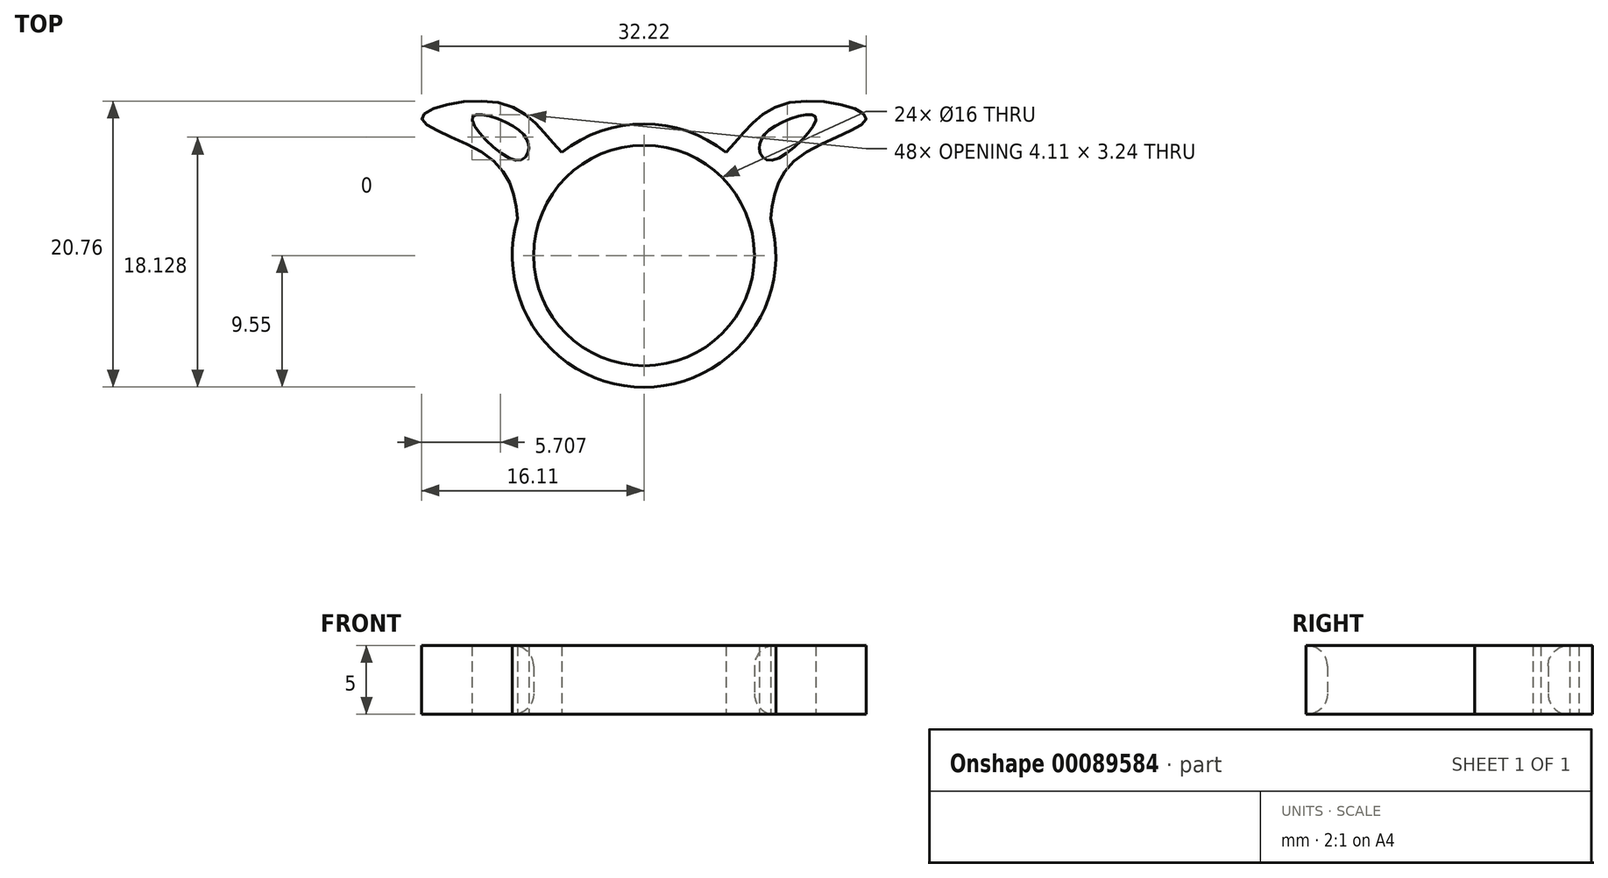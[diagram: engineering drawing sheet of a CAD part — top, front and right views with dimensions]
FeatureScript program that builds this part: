
annotation { "Feature Type Name" : "Feature", "Feature Type Description" : "" }
export const myFeature = defineFeature(function(context is Context, id is Id, definition is map)
    precondition{}
    {
        {
            var Q0;
            Q0=qCreatedBy(makeId("Top.planeOp"),FACE);
            var sketch = newSketch(context, id + "F0", { "sketchPlane" : qUnion([Q0])});
            skCircle(sketch, "E0", {"center": v(0, 0) * mm, "radius": 8 * mm});
            skCircle(sketch, "E1", {"center": v(0, 0) * mm, "radius": 9.55 * mm});
            skFitSpline(sketch, "E2", {"points": [v(-9.17, 2.68) * mm, v(-11.22, 7.13) * mm, v(-16.1, 10) * mm, v(-10.37, 11.05) * mm, v(-5.95, 7.47) * mm], "startDerivative": vector(-2, 20.05) * mm, "endDerivative": vector(15.12, -15.38) * mm});
            skFitSpline(sketch, "E3.MirrorCS", {"points": [v(9.17, 2.68) * mm, v(11.22, 7.13) * mm, v(16.1, 10) * mm, v(10.37, 11.05) * mm, v(5.95, 7.47) * mm], "startDerivative": vector(2, 20.05) * mm, "endDerivative": vector(-15.12, -15.38) * mm});
            skSolve(sketch);
        }
        {
            var Q0;
            Q0 = qSketchRegion(id + "F0", true);
            extrude(context, id + "F1", {"entities" : qUnion([Q0]), "depth" : 5 * mm});
        }
        {
            var Q0;
            Q0=makeQuery(id+"F1.opExtrude","CAP_EDGE",EDGE,{"disambiguationData":[OSD([sQuery(id+"F0.wireOp",EDGE,"E0")])],"isStart":false});
            var Q1;
            Q1=makeQuery(id+"F1.opExtrude","CAP_EDGE",EDGE,{"disambiguationData":[OSD([sQuery(id+"F0.wireOp",EDGE,"E0")])],"isStart":true});
            fillet(context, id + "F2", {"entities" : qUnion([Q0, Q1]), "radius" : 1.5 * mm, "tangentPropagation" : true, "allowEdgeOverflow" : false});
        }
        {
            var Q0;
            Q0=makeQuery(id+"F1.opExtrude","CAP_FACE",FACE,{"disambiguationData":[OSD([sQuery(id+"F0.wireOp",EDGE,"E0"),sQuery(id+"F0.wireOp",EDGE,"E1"),sQuery(id+"F0.wireOp",EDGE,"E2"),sQuery(id+"F0.wireOp",EDGE,"E3.MirrorCS")])],"isStart":false});
            var sketch = newSketch(context, id + "F3", { "sketchPlane" : qUnion([Q0])});
            skFitSpline(sketch, "E4", {"points": [v(-8.35, 7.75) * mm, v(-9.64, 9.48) * mm, v(-12.45, 10) * mm, v(-9.31, 6.92) * mm, v(-8.35, 7.75) * mm]});
            skLineSegment(sketch, "E5", {"start": v(0, 0) * mm, "end": v(0, 13.5) * mm});
            skFitSpline(sketch, "E6.MirrorC", {"points": [v(8.35, 7.75) * mm, v(9.64, 9.48) * mm, v(12.45, 10) * mm, v(9.31, 6.92) * mm, v(8.35, 7.75) * mm]});
            skSolve(sketch);
        }
        {
            var Q0;
            Q0 = qSketchRegion(id + "F3", true);
            extrude(context, id + "F4", {"entities" : qUnion([Q0]), "operationType" : NewBodyOperationType.REMOVE, "oppositeDirection" : true, "depth" : 25 * mm});
        }
    });
